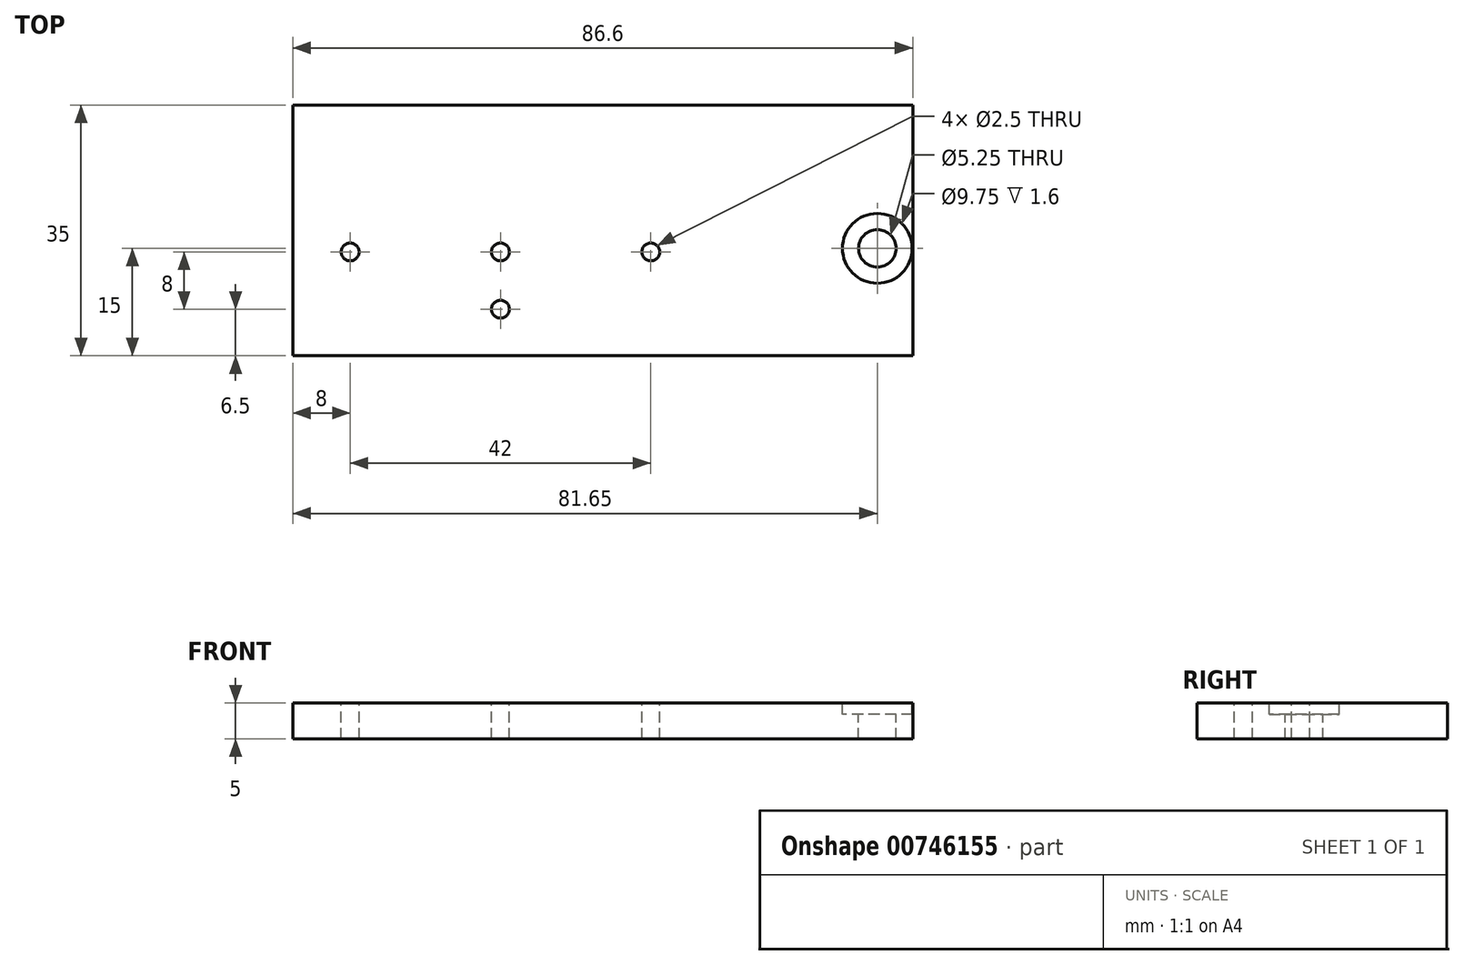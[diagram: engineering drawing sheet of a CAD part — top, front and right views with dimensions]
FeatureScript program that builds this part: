
annotation { "Feature Type Name" : "Feature", "Feature Type Description" : "" }
export const myFeature = defineFeature(function(context is Context, id is Id, definition is map)
    precondition{}
    {
        {
            var Q0;
            Q0=qCreatedBy(makeId("Front.planeOp"),FACE);
            var sketch = newSketch(context, id + "F0", { "sketchPlane" : qUnion([Q0])});
            skLineSegment(sketch, "E0", {"start": v(-46, 0) * mm, "end": v(46, 0) * mm});
            skLineSegment(sketch, "E1", {"start": v(46, 0) * mm, "end": v(46, 5) * mm});
            skLineSegment(sketch, "E2", {"start": v(46, 5) * mm, "end": v(-46, 5) * mm});
            skLineSegment(sketch, "E3", {"start": v(-46, 5) * mm, "end": v(-46, 0) * mm});
            skSolve(sketch);
        }
        {
            var Q0;
            Q0=makeQuery(id+"F0.imprint","IMPRINT",FACE,{"disambiguationData":[TD([[makeQuery(id+"F0.imprint","IMPRINT",EDGE,{"derivedFrom":sQuery(id+"F0.wireOp",EDGE,"E0")}),1.0]])]});
            extrude(context, id + "F1", {"entities" : qUnion([Q0]), "depth" : 35 * mm, "offsetDistance" : 25 * mm});
        }
        {
            var Q0;
            Q0=makeQuery(id+"F1.opExtrude","SWEPT_FACE",FACE,{"disambiguationData":[OSD([sQuery(id+"F0.wireOp",EDGE,"E2")])]});
            var sketch = newSketch(context, id + "F2", { "sketchPlane" : qUnion([Q0])});
            skPoint(sketch, "E4", {"position": v(35.65, -20) * mm});
            skLineSegment(sketch, "E5", {"start": v(35.65, -20) * mm, "end": v(35.65, 0) * mm, "construction": true});
            skLineSegment(sketch, "E6", {"start": v(35.65, -15) * mm, "end": v(35.65, -35) * mm, "construction": true});
            skLineSegment(sketch, "E7", {"start": v(12, 0) * mm, "end": v(12, -35) * mm, "construction": true});
            skPoint(sketch, "E8", {"position": v(-17, -28.5) * mm});
            skPoint(sketch, "E9", {"position": v(-38, -20.5) * mm});
            skPoint(sketch, "E10", {"position": v(-17, -20.5) * mm});
            skPoint(sketch, "E11", {"position": v(4, -20.5) * mm});
            skLineSegment(sketch, "E12", {"start": v(-41.14, -20.5) * mm, "end": v(5.88, -20.5) * mm, "construction": true});
            skLineSegment(sketch, "E13", {"start": v(-17, -28.5) * mm, "end": v(12, -28.5) * mm, "construction": true});
            skLineSegment(sketch, "E14", {"start": v(12, -28.5) * mm, "end": v(-46, -28.5) * mm, "construction": true});
            skLineSegment(sketch, "E15", {"start": v(40.6, 0) * mm, "end": v(40.6, -35) * mm});
            skSolve(sketch);
        }
        {
            var Q0;
            Q0=sQuery(id+"F2.wireOp",VERTEX,"E4");
            var Q1;
            Q1=makeQuery(id+"F1.opExtrude","SWEPT_BODY",BODY,{"disambiguationData":[OSD([sQuery(id+"F0.wireOp",EDGE,"E0"),sQuery(id+"F0.wireOp",EDGE,"E1"),sQuery(id+"F0.wireOp",EDGE,"E2"),sQuery(id+"F0.wireOp",EDGE,"E3")])]});
            hole(context, id + "F3", {"style" : HoleStyle.C_BORE, "endStyle" : HoleEndStyle.BLIND, "holeDiameter" : 5.25 * mm, "cBoreDiameter" : 9.75 * mm, "cBoreDepth" : 1.6 * mm, "majorDiameter" : 5 * mm, "holeDepth" : 5 * mm, "isTappedThrough" : true, "tappedDepth" : 12 * mm, "tapClearance" : 3, "startFromSketch" : true, "locations" : qUnion([Q0]), "scope" : qUnion([Q1])});
        }
        {
            var Q0;
            Q0=sQuery(id+"F2.wireOp",VERTEX,"E9");
            var Q1;
            Q1=sQuery(id+"F2.wireOp",VERTEX,"E10");
            var Q2;
            Q2=sQuery(id+"F2.wireOp",VERTEX,"E11");
            var Q3;
            Q3=sQuery(id+"F2.wireOp",VERTEX,"E8");
            var Q4;
            Q4=makeQuery(id+"F1.opExtrude","SWEPT_BODY",BODY,{"disambiguationData":[OSD([sQuery(id+"F0.wireOp",EDGE,"E0"),sQuery(id+"F0.wireOp",EDGE,"E1"),sQuery(id+"F0.wireOp",EDGE,"E2"),sQuery(id+"F0.wireOp",EDGE,"E3")])]});
            hole(context, id + "F4", {"style" : HoleStyle.SIMPLE, "endStyle" : HoleEndStyle.BLIND, "standardTappedOrClearance" : lookupTablePath({ "standard" : "ISO", "engagement" : "75%", "pitch" : "0.5 mm", "size" : "M3", "type" : "Tapped" }), "standardBlindInLast" : lookupTablePath({ "standard" : "ISO", "engagement" : "75%", "pitch" : "0.5 mm", "size" : "M3", "type" : "Tapped" }), "holeDiameter" : 2.5 * mm, "majorDiameter" : 3 * mm, "showTappedDepth" : true, "holeDepth" : 13.5 * mm, "isTappedThrough" : true, "tappedDepth" : 12 * mm, "tapClearance" : 3, "locations" : qUnion([Q0, Q1, Q2, Q3]), "scope" : qUnion([Q4])});
        }
        {
            var Q0;
            {var subQ0=sQuery(id+"F2.wireOp",EDGE,"E15");Q0=makeQuery(id+"F2.imprint","IMPRINT",FACE,{"disambiguationData":[TD([[makeQuery(id+"F2.imprint","IMPRINT",EDGE,{"derivedFrom":subQ0}),1.0]])]});}
            extrude(context, id + "F5", {"entities" : qUnion([Q0]), "operationType" : NewBodyOperationType.REMOVE, "oppositeDirection" : true, "depth" : 5 * mm, "offsetDistance" : 25 * mm});
        }
    });
